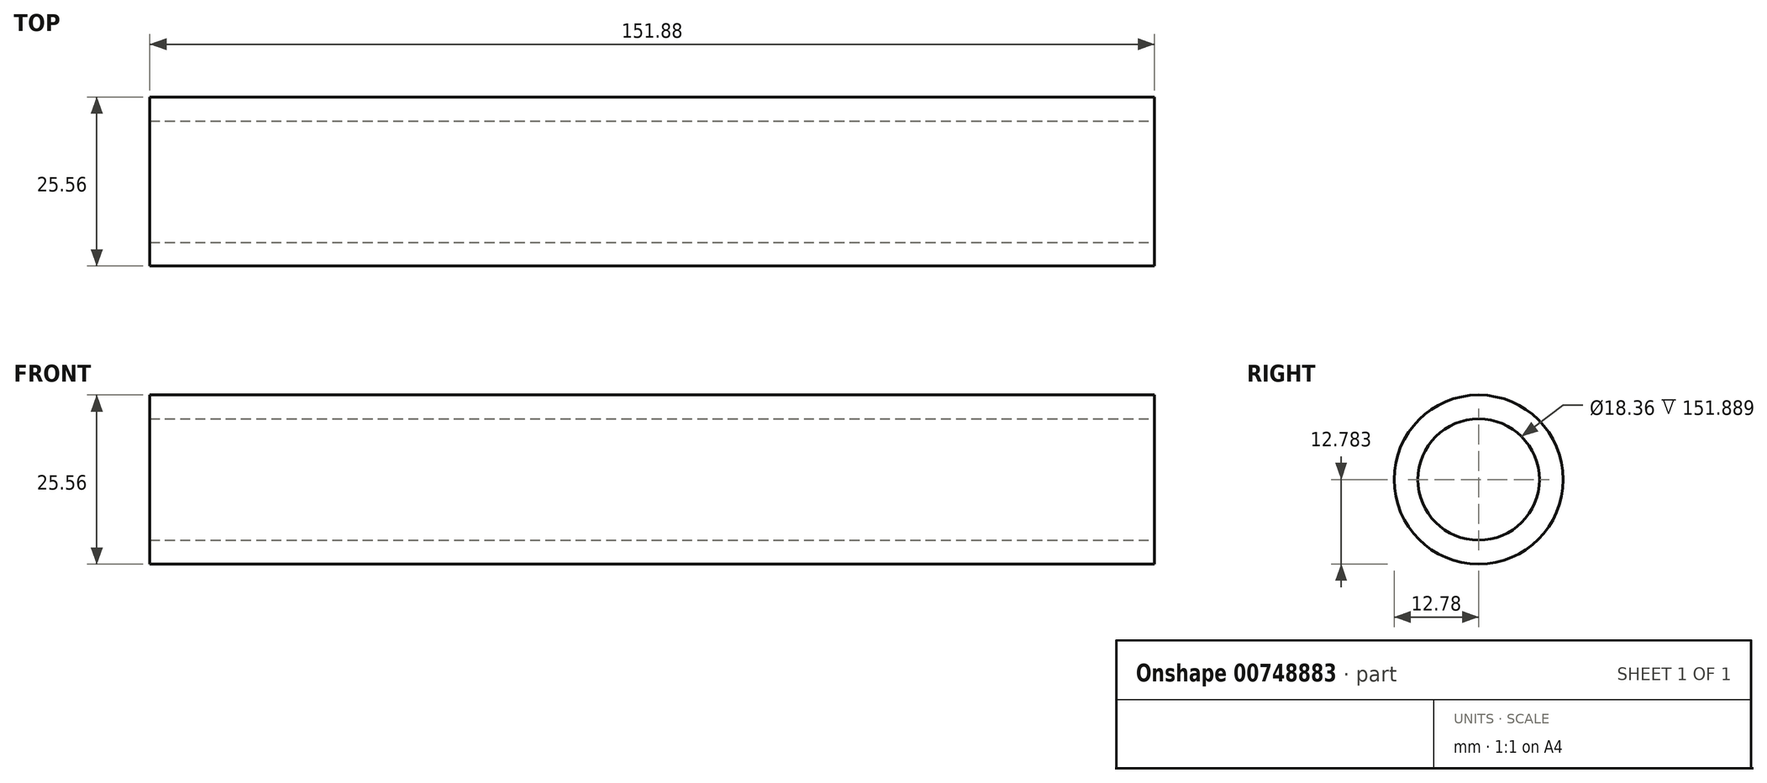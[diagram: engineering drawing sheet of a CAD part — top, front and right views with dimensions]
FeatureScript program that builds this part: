
annotation { "Feature Type Name" : "Feature", "Feature Type Description" : "" }
export const myFeature = defineFeature(function(context is Context, id is Id, definition is map)
    precondition{}
    {
        {
            var Q0;
            Q0=qCreatedBy(makeId("Front.planeOp"),FACE);
            var sketch = newSketch(context, id + "F0", { "sketchPlane" : qUnion([Q0])});
            skLineSegment(sketch, "E0", {"start": v(-75.94, 21.5) * mm, "end": v(-75.94, 8.71) * mm});
            skLineSegment(sketch, "E1", {"start": v(-75.94, 8.71) * mm, "end": v(75.94, 8.71) * mm});
            skLineSegment(sketch, "E2", {"start": v(75.94, 8.71) * mm, "end": v(75.94, 21.5) * mm});
            skLineSegment(sketch, "E3", {"start": v(75.94, 21.5) * mm, "end": v(-75.94, 21.5) * mm});
            skSolve(sketch);
        }
        {
            var Q0;
            Q0=makeQuery(id+"F0.imprint","IMPRINT",FACE,{"disambiguationData":[TD([[makeQuery(id+"F0.imprint","IMPRINT",EDGE,{"derivedFrom":sQuery(id+"F0.wireOp",EDGE,"E0")}),1.0]])]});
            var Q1;
            Q1=sQuery(id+"F0.wireOp",EDGE,"E1");
            revolve(context, id + "F1", {"surfaceOperationType" : NewSurfaceOperationType.NEW, "entities" : qUnion([Q0]), "axis" : qUnion([Q1]), "revolveType" : RevolveType.FULL});
        }
        {
            var Q0;
            Q0=makeQuery(id+"F1.opRevolve","SWEPT_FACE",FACE,{"disambiguationData":[OSD([sQuery(id+"F0.wireOp",EDGE,"E2")])]});
            var sketch = newSketch(context, id + "F2", { "sketchPlane" : qUnion([Q0])});
            skCircle(sketch, "E4", {"center": v(0, 8.71) * mm, "radius": 9.18 * mm});
            skSolve(sketch);
        }
        {
            var Q0;
            Q0=makeQuery(id+"F2.imprint","IMPRINT",FACE,{"disambiguationData":[TD([[makeQuery(id+"F2.imprint","IMPRINT",EDGE,{"derivedFrom":sQuery(id+"F2.wireOp",EDGE,"E4")}),1.0]])]});
            extrude(context, id + "F3", {"entities" : qUnion([Q0]), "operationType" : NewBodyOperationType.REMOVE, "oppositeDirection" : true, "depth" : 162.8 * mm, "offsetDistance" : 25.4 * mm});
        }
    });
